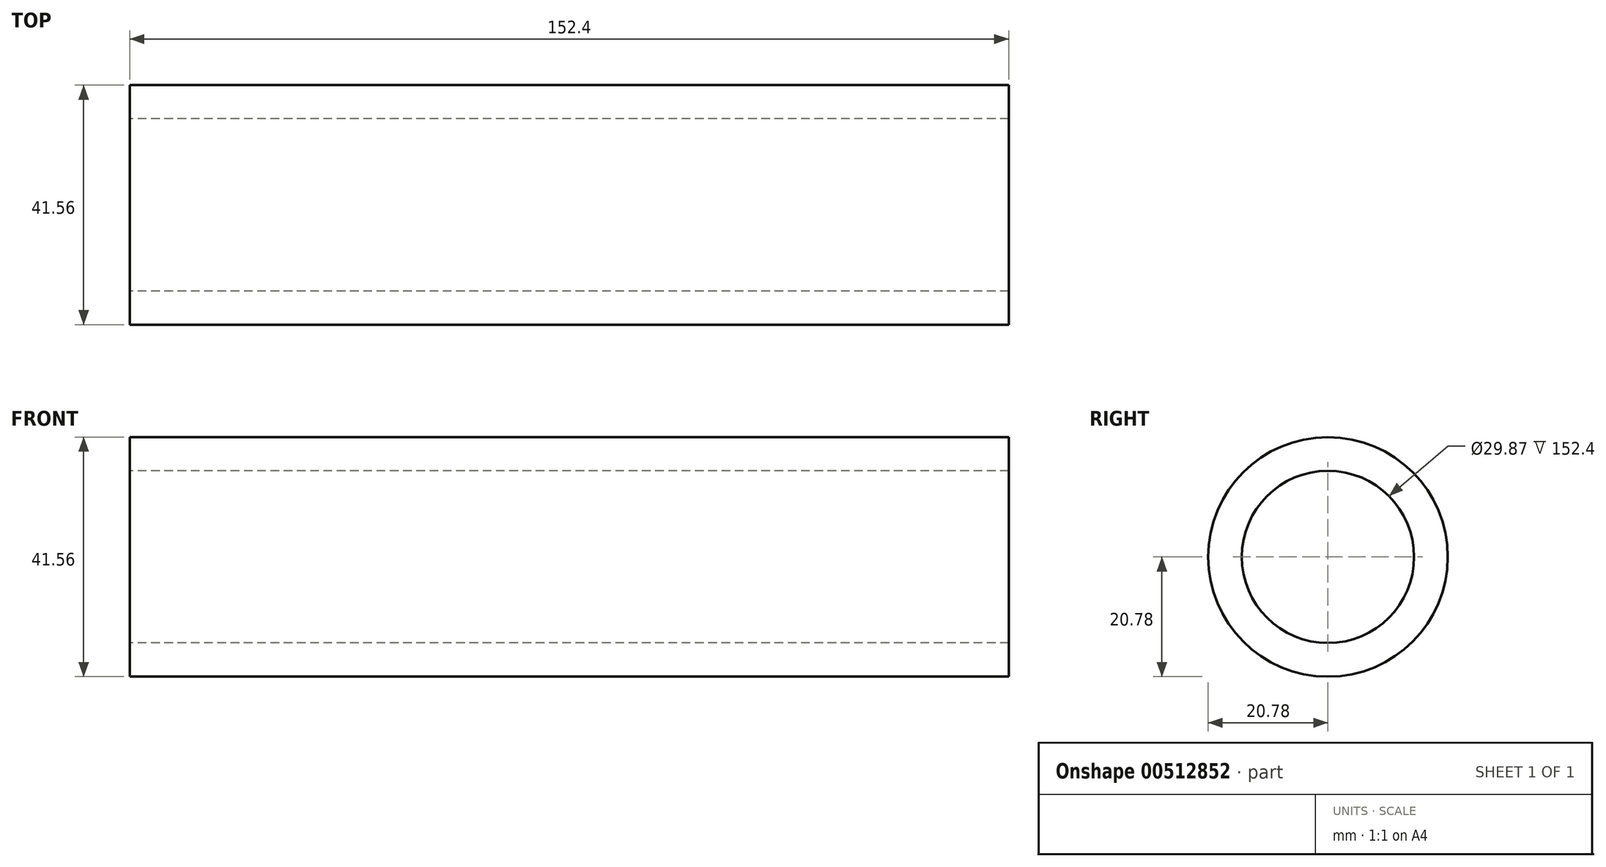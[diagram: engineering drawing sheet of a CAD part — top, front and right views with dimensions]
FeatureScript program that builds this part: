
annotation { "Feature Type Name" : "Feature", "Feature Type Description" : "" }
export const myFeature = defineFeature(function(context is Context, id is Id, definition is map)
    precondition{}
    {
        {
            var Q0;
            Q0=qCreatedBy(makeId("Right.planeOp"),FACE);
            var sketch = newSketch(context, id + "F0", { "sketchPlane" : qUnion([Q0])});
            skCircle(sketch, "E0", {"center": v(0, 0) * mm, "radius": 20.78 * mm});
            skCircle(sketch, "E1", {"center": v(0, 0) * mm, "radius": 14.93 * mm});
            skSolve(sketch);
        }
        {
            var Q0;
            Q0 = qSketchRegion(id + "F0", true);
            extrude(context, id + "F1", {"entities" : qUnion([Q0]), "depth" : 152.4 * mm});
        }
    });
